# Revit family: 2060535 Sylvania Lighting Fixture ASCENT100 II ARCH 2000 4K STD 120
name_source: partatom
category: Lighting Fixtures
revit_build: Autodesk Revit 2016 (Build: 20150220_1215(x64)
units: mm (PartAtom-declared; Revit-internal decimal feet)

## family parameters
Cut with Voids When Loaded = No
Host = Face
Light Source = Yes
OmniClass Number = 23.80.70.11.17
OmniClass Title = Specialized Lighting by Location or Use
Part Type = Normal
Room Calculation Point = No
Round Connector Dimension = Use Diameter
Shared = No

## types (1)
- 2060535 ASCT100 II ARCH 2000 4K STD 120
    Aperture_SYL = 120 mm
    Apparent Load = 18 VA
    Assembly Code = D5020200
    AssetType = Fixed
    Color Filter = 16777215
    CutoutDiameter_SYL = 137 mm  [stored 0.449475 ft]
    Default Elevation = 0 mm  [stored 0 ft]
    Description = Direct LED retro fit for original LED 100 Arch (120) single CFL lamp offering Matching lumen levels and improved light distribution of original LED 100 CFL lamp equivalents Typically half the power consumption compared to CFL Up to 104lm/W 120mm aperture Architectural reflector accepts range of glass accessories from existing LED 100 Arch 120 offering HE, HO and VHO versions equivalent of single 1 x 13W, 1 x 18W, 1 x 26W Additional VVHO versions which offer the performance circa 2 x 26W equivalent
    Diameter_SYL = 150 mm
    DiffuserRadius_SYL = 53 mm  [stored 0.173885 ft]
    Dimming Lamp Color Temperature Shift = <None>
    DocumentationLiterature = http://www.sylvania-lighting.com
    DurationUnit = hours
    ElectricShockClassification = Class II
    Emit Shape Visible in Rendering = No
    Emit from Circle Diameter = 106 mm  [stored 0.347769 ft]
    ExpectedLife = 50000
    Height_SYL = 94 mm  [stored 0.308399 ft]
    IfcExportAs = IfcLightFixtureType
    IfcExportType = IfcLightFixtureType
    ImpactProtectionIndex = IK02
    IngressProtection = IP40
    Keynote = 16500
    Lamp = LED
    LampColourRenderingIndex = 80
    LampColourTemperature = 4000 K
    LampNominalLuminous = 2029 lm
    LampsType = LED
    LightOutputRatio = 100
    LuminousEfficacy = 113 lm/W
    Manufacturer = Feilo Sylvania
    ManufacturerName = Feilo Sylvania
    Material = aluminium housing, acrylic diffuser
    Material_1_SYL = Aluminum_Sylvania_Ascent_White
    Material_2_SYL = Aluminum_Sylvania_Ascent_White
    Material_3_SYL = Polycarbonate_Sylvania_Ascent_Clear
    Material_4_SYL = Aluminium_Sylvania_Ascent_Silver
    Model = ASCENT100 II ARCH 2000 4K STD 120
    ModelNumber = 2060535
    ModelReference = ASCENT100 II ARCH 2000 4K STD 120
    Name = ASCENT100 II ARCH 2000 4K STD 120
    NominalHeight = 94 mm  [stored 0.308399 ft]
    NominalLength = 0 mm  [stored 0 ft]
    NominalWidth = 0 mm  [stored 0 ft]
    Photometric Web File = 2060535.ies
    PowerConsumption = 18 W
    PowerFactor = 0
    Radius_SYL = 75 mm
    ReflectorRadius_SYL = 60 mm  [stored 0.19685 ft]
    Tilt Angle = -90°
    TypeName = ASCENT100 II ARCH 2000 4K STD 120
    URL = http://www.sylvania-lighting.com
    Voltage = 0 V
    Weight = 0.715 kg

note: [stored X ft] marks values corroborated as IEEE doubles in the binary element streams (Revit-internal decimal feet)

## geometry (parser evidence)
native form markers: Sweep x3
no freeform markers — native parametric forms only
